# Revit family: Access_Door-Adjustable-Access-Best Access Doors-BA-RADJ
name_source: partatom
category: Specialty Equipment
revit_build: Autodesk Revit 2017 (Build: 20160225_1515(x64)
units: mm (PartAtom-declared; Revit-internal decimal feet)

## family parameters
Cut with Voids When Loaded = No
Host = Face
OmniClass Number = 23.30.10.27.17
Part Type = Normal
Room Calculation Point = No
Round Connector Dimension = Use Diameter
Shared = No

## types (6) — shared parameters
Assembly Code = C1020700
Construction Material = Metal - Best Access Doors - Aluminum
Default Elevation = 0"
Description = Adjustable Access Door
Finish = Metal - Best Access Doors - Powder Coated White
Frame Depth = 1 11/32"
Manufacturer = Best Access Doors
Model = BA-RADJ
Product data url = https://bimobject.com
URL = https://www.bestaccessdoors.com

## per-type parameters (varying)
| type | Door Height | Door Height Calc | Door Open | Door Width | Door Width Calc | Height Actual | Width Actual |
| Custom | 12" | 12" | No | 12" | 12" | 12" | 12" |
| 6 x 7.5 | 7 1/2" | 7 1/2" | No | 6" | 6" | 7 1/2" | 6" |
| 8 x 9.5 | 9 1/2" | 9 1/2" | No | 8" | 8" | 9 1/2" | 8" |
| 10 x 11.5 | 11 1/2" | 11 1/2" | Yes | 10" | 10" | 11 1/2" | 10" |
| 12 x 13.5 | 13 1/2" | 13 1/2" | No | 12" | 12" | 13 1/2" | 12" |
| 14 x 15.5 | 15 1/2" | 15 1/2" | No | 14" | 14" | 15 1/2" | 14" |

## geometry (parser evidence)
native form markers: Blend x4, Sweep x12
no freeform markers — native parametric forms only
